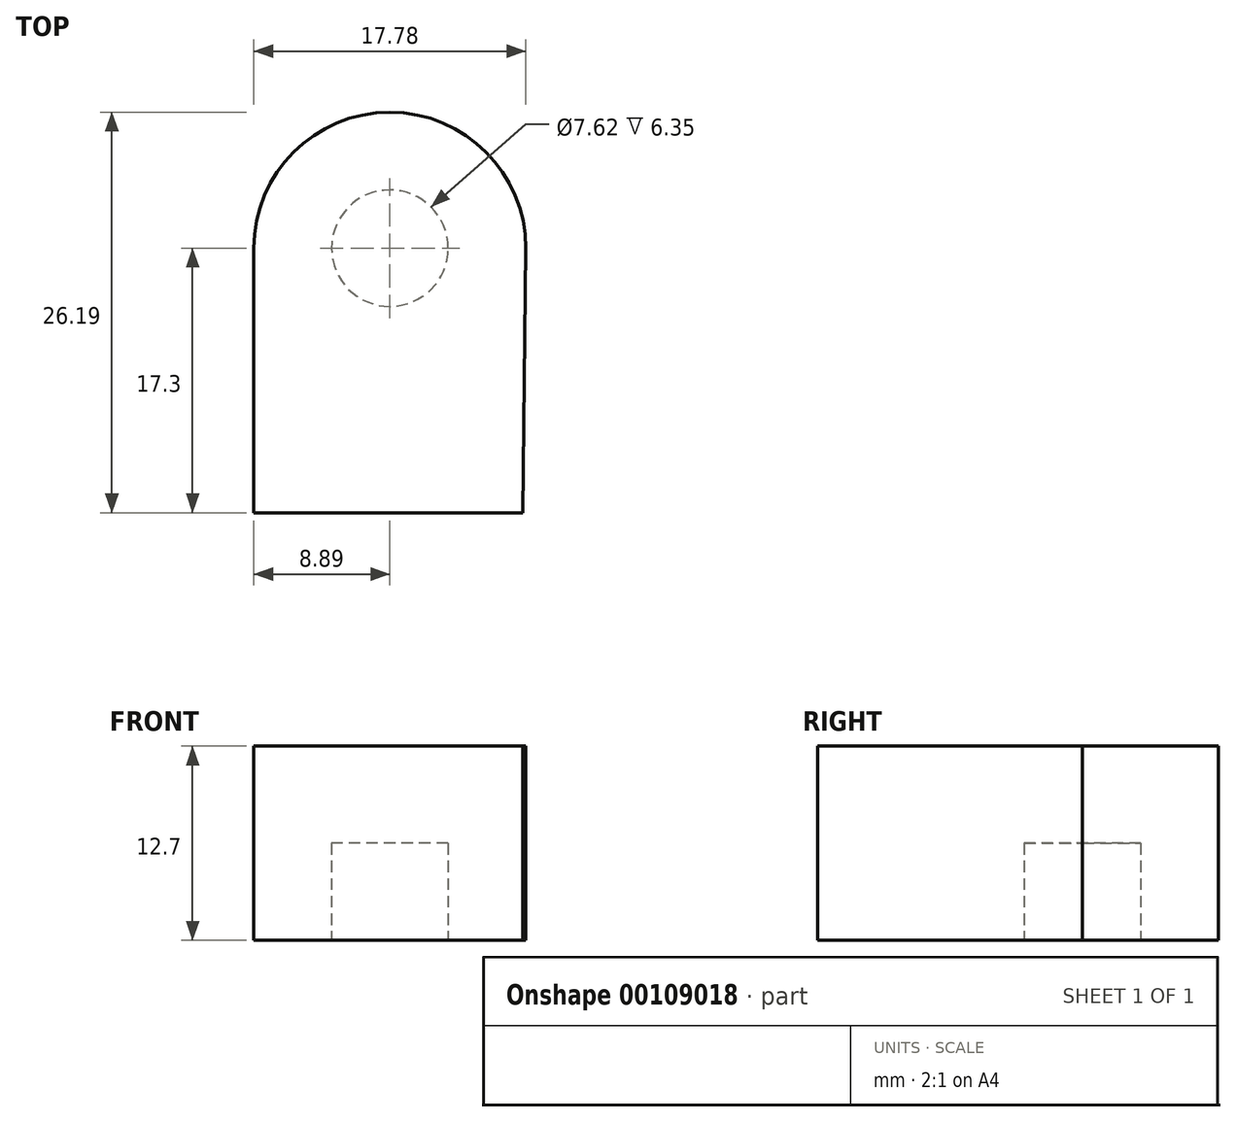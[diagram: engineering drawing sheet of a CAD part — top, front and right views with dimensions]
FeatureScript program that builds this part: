
annotation { "Feature Type Name" : "Feature", "Feature Type Description" : "" }
export const myFeature = defineFeature(function(context is Context, id is Id, definition is map)
    precondition{}
    {
        {
            var Q0;
            Q0=qCreatedBy(makeId("Top.planeOp"),FACE);
            var sketch = newSketch(context, id + "F0", { "sketchPlane" : qUnion([Q0])});
            skCircle(sketch, "E0", {"center": v(0, 0) * mm, "radius": 3.81 * mm});
            skArc(sketch, "E1", {"start": v(8.89, -0.21) * mm, "mid": v(0.1, 8.89) * mm, "end": v(-8.9, 0) * mm});
            skLineSegment(sketch, "E2", {"start": v(-8.9, 0) * mm, "end": v(-8.9, -17.3) * mm});
            skLineSegment(sketch, "E3", {"start": v(-8.9, -17.3) * mm, "end": v(8.68, -17.3) * mm});
            skLineSegment(sketch, "E4", {"start": v(8.9, 0) * mm, "end": v(8.68, -17.3) * mm});
            skSolve(sketch);
        }
        {
            var Q0;
            Q0=makeQuery(id+"F0.imprint","IMPRINT",FACE,{"disambiguationData":[TD([[makeQuery(id+"F0.imprint","IMPRINT",EDGE,{"derivedFrom":sQuery(id+"F0.wireOp",EDGE,"E0")}),-1.0]])]});
            var Q1;
            Q1=makeQuery(id+"F0.imprint","IMPRINT",FACE,{"disambiguationData":[TD([[makeQuery(id+"F0.imprint","IMPRINT",EDGE,{"derivedFrom":sQuery(id+"F0.wireOp",EDGE,"E0")}),1.0]])]});
            extrude(context, id + "F1", {"entities" : qUnion([Q0, Q1]), "depth" : 12.7 * mm});
        }
        {
            var Q0;
            Q0=makeQuery(id+"F0.imprint","IMPRINT",FACE,{"disambiguationData":[TD([[makeQuery(id+"F0.imprint","IMPRINT",EDGE,{"derivedFrom":sQuery(id+"F0.wireOp",EDGE,"E0")}),1.0]])]});
            extrude(context, id + "F2", {"entities" : qUnion([Q0]), "operationType" : NewBodyOperationType.REMOVE, "depth" : 6.35 * mm});
        }
    });
